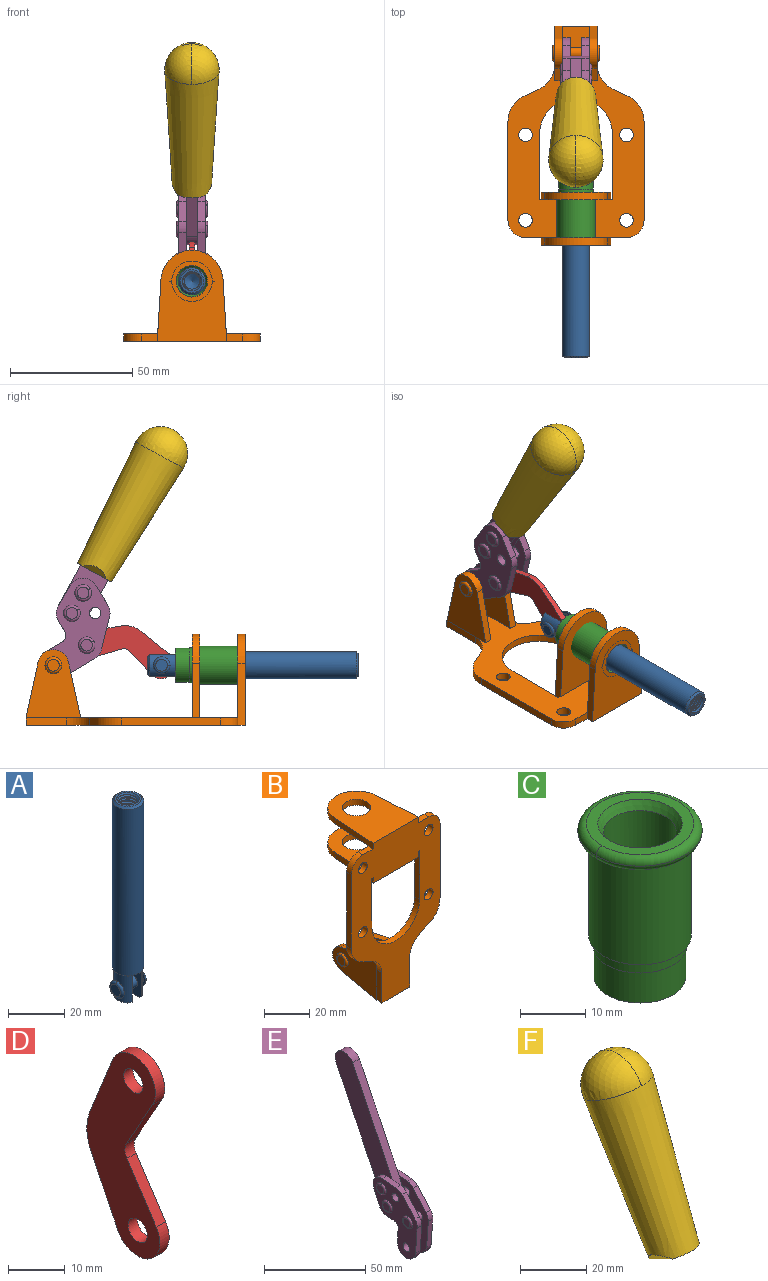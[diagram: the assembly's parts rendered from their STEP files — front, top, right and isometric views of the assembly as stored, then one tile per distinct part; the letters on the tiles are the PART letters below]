
ASSEMBLY  parts=6 mates=6
PART A: 48 faces, bbox 12.6x11.1x86.1 mm
  f0: torus R=2.41mm, axis (-1,0,0), area 15mm2, adj f30,f32,f34
  f1: torus R=2.41mm, axis (-1,0,0), area 15mm2, adj f29,f31,f33
  f2: cylinder r=5.54mm len=72.39mm, axis (0,0,1), area 2518.5mm2, adj f3,f4,f42,f43
  f3: cone r=5.54mm half-angle=45deg, axis (0,0,1), area 7.6mm2, adj f2,f5,f41
  f4: cone r=5.54mm half-angle=45deg, axis (0,0,-1), area 34.9mm2, adj f2,f39
  f5: cylinder r=5.08mm len=11.48mm, axis (0,0,1), area 108.3mm2, adj f3,f7,f8,f41
  f6: cylinder r=2.41mm len=4.83mm, axis (-1,0,0), area 71.2mm2, adj f40,f41
  f7: cylinder r=2.41mm len=4.83mm, axis (-1,0,0), area 7.6mm2, adj f5,f34
  f8: cone r=5.08mm half-angle=45deg, axis (0,0,1), area 10.6mm2, adj f5,f37,f41
  f9: cone r=3.98mm half-angle=45deg, axis (0,0,1), area 17.6mm2, adj f27,f39,f45,f46,f47
  f10: cylinder r=2.41mm len=4.83mm, axis (-1,0,0), area 7.6mm2, adj f33,f38
  f11: cylinder r=3.2mm len=6.4mm, axis (0,0,1), area 78.4mm2, adj f12,f28,f44,f45,f47
  f12: cylinder r=3.2mm len=6.4mm, axis (0,0,1), area 10.5mm2, adj f11,f13,f45,f47
  f13: cylinder r=3.2mm len=6.4mm, axis (0,0,1), area 10.5mm2, adj f12,f14,f45,f47
  f14: cylinder r=3.2mm len=6.4mm, axis (0,0,1), area 10.5mm2, adj f13,f15,f45,f47
  f15: cylinder r=3.2mm len=6.4mm, axis (0,0,1), area 10.5mm2, adj f14,f16,f45,f47
  f16: cylinder r=3.2mm len=6.4mm, axis (0,0,1), area 10.5mm2, adj f15,f17,f45,f47
  f17: cylinder r=3.2mm len=6.4mm, axis (0,0,1), area 10.5mm2, adj f16,f18,f45,f47
  f18: cylinder r=3.2mm len=6.4mm, axis (0,0,1), area 10.5mm2, adj f17,f19,f45,f47
  f19: cylinder r=3.2mm len=6.4mm, axis (0,0,1), area 10.5mm2, adj f18,f20,f45,f47
  f20: cylinder r=3.2mm len=6.4mm, axis (0,0,1), area 10.5mm2, adj f19,f21,f45,f47
  f21: cylinder r=3.2mm len=6.4mm, axis (0,0,1), area 10.5mm2, adj f20,f22,f45,f47
  f22: cylinder r=3.2mm len=6.4mm, axis (0,0,1), area 10.5mm2, adj f21,f23,f45,f47
  f23: cylinder r=3.2mm len=6.4mm, axis (0,0,1), area 10.5mm2, adj f22,f24,f45,f47
  f24: cylinder r=3.2mm len=6.4mm, axis (0,0,1), area 10.5mm2, adj f23,f25,f45,f47
  f25: cylinder r=3.2mm len=6.4mm, axis (0,0,1), area 10.5mm2, adj f24,f26,f45,f47
  f26: cylinder r=3.2mm len=6.4mm, axis (0,0,1), area 10.5mm2, adj f25,f27,f45,f47
  f27: cylinder r=3.2mm len=6.4mm, axis (0,0,1), area 7.4mm2, adj f9,f26,f45,f47
  f28: cone r=3.2mm half-angle=60deg, axis (0,0,1), area 37.2mm2, adj f11
  f29: plane 4.83x4.83mm, normal (-1,0,0), area 18.3mm2, adj f1,f31
  f30: plane 4.83x4.83mm, normal (1,0,0), area 18.3mm2, adj f0,f32
  f31: torus R=2.41mm, axis (-1,0,0), area 15mm2, adj f1,f29,f33
  f32: torus R=2.41mm, axis (-1,0,0), area 15mm2, adj f0,f30,f34
  f33: plane 6.83x6.83mm, normal (1,0,0), area 18.3mm2, adj f1,f10,f31
  f34: plane 6.83x6.83mm, normal (-1,0,0), area 18.3mm2, adj f0,f7,f32
  f35: cone r=5.08mm half-angle=45deg, axis (0,0,1), area 10.6mm2, adj f36,f38,f40
  f36: plane 7.25x1.97mm, normal (0,0,-1), area 10mm2, adj f35,f40
  f37: plane 7.25x1.97mm, normal (0,0,-1), area 10mm2, adj f8,f41
  f38: cylinder r=5.08mm len=11.48mm, axis (0,0,1), area 108.3mm2, adj f10,f35,f40,f42
  f39: plane 9.55x9.55mm, normal (0,0,1), area 22mm2, adj f4,f9
  f40: plane 12.76x10.09mm, normal (1,0,0), area 95.7mm2, adj f6,f35,f36,f38,f42,f43
  f41: plane 12.76x10.09mm, normal (-1,0,0), area 95.7mm2, adj f3,f5,f6,f8,f37,f43
  f42: cone r=5.54mm half-angle=45deg, axis (0,0,1), area 7.6mm2, adj f2,f38,f40
  f43: plane 11.07x4.7mm, normal (0,0,-1), area 50.4mm2, adj f2,f40,f41
  f44: plane 0.89x0.62mm, normal (-1,0,0), area 0.3mm2, adj f11,f45,f46,f47
  f45: bspline ~24.8x7.63mm, area 266.6mm2, adj f9,f11,f12,f13,f14,f15,f16,f17
  f46: bspline ~24.87x7.63mm, area 73.6mm2, adj f9,f44,f45,f47
  f47: bspline ~24.98x7.63mm, area 272.5mm2, adj f9,f11,f12,f13,f14,f15,f16,f17
PART B: 55 faces, bbox 55.7x37.4x89.8 mm
  f0: torus R=2.41mm, axis (-1,0,0), area 15mm2, adj f11,f15,f25
  f1: torus R=2.41mm, axis (-1,0,0), area 15mm2, adj f10,f12,f22
  f2: cylinder r=2.78mm len=5.56mm, axis (0,-1,0), area 54.2mm2, adj f30,f54
  f3: cylinder r=14.99mm len=29.97mm, axis (0,-1,0), area 145.9mm2, adj f30,f49,f53,f54
  f4: cylinder r=2.78mm len=5.56mm, axis (0,-1,0), area 54.2mm2, adj f30,f54
  f5: cylinder r=2.78mm len=5.56mm, axis (0,-1,0), area 54.2mm2, adj f30,f54
  f6: cylinder r=2.78mm len=5.56mm, axis (0,-1,0), area 54.2mm2, adj f30,f54
  f7: cylinder r=6.35mm len=12.7mm, axis (0,0,1), area 123.6mm2, adj f27,f51
  f8: cylinder r=6.35mm len=12.7mm, axis (0,0,-1), area 124.7mm2, adj f21,f35
  f9: cylinder r=2.41mm len=11.18mm, axis (-1,0,0), area 169.4mm2, adj f16,f19
  f10: plane 4.83x4.83mm, normal (1,0,0), area 18.3mm2, adj f1,f12
  f11: plane 4.83x4.83mm, normal (-1,0,0), area 18.3mm2, adj f0,f15
  f12: torus R=2.41mm, axis (-1,0,0), area 15mm2, adj f1,f10,f22
  f13: cylinder r=6.35mm len=12.41mm, axis (1,0,0), area 53.4mm2, adj f18,f19,f22,f23
  f14: cylinder r=6.35mm len=12.41mm, axis (-1,0,0), area 53.4mm2, adj f16,f17,f24,f25
  f15: torus R=2.41mm, axis (-1,0,0), area 15mm2, adj f0,f11,f25
  f16: plane 27.86x22.35mm, normal (1,0,0), area 425.4mm2, adj f9,f14,f17,f24,f30
  f17: plane 22.86x4.97mm, normal (0,0.21,0.98), area 72.5mm2, adj f14,f16,f25,f30
  f18: plane 22.86x4.97mm, normal (0,0.21,0.98), area 72.5mm2, adj f13,f19,f22,f30
  f19: plane 27.86x22.35mm, normal (-1,0,0), area 425.4mm2, adj f9,f13,f18,f23,f30
  f20: cylinder r=12.7mm len=25.35mm, axis (0,0,-1), area 119.8mm2, adj f21,f34,f35,f36
  f21: plane 34.21x28.07mm, normal (0,0,-1), area 702.4mm2, adj f8,f20,f30,f34,f36
  f22: plane 27.96x22.45mm, normal (1,0,0), area 407.2mm2, adj f1,f12,f13,f18,f23,f30,f42,f43
  f23: plane 22.86x4.97mm, normal (0,0.21,-0.98), area 72.5mm2, adj f13,f19,f22,f44
  f24: plane 22.86x4.97mm, normal (0,0.21,-0.98), area 72.5mm2, adj f14,f16,f25,f44
  f25: plane 27.86x22.35mm, normal (-1,0,0), area 407.1mm2, adj f0,f14,f15,f17,f24,f30,f45,f46
  f26: plane 3.1x0.95mm, normal (0,0,-1), area 2.7mm2, adj f30,f49,f50,f54
  f27: plane 34.21x28.07mm, normal (0,0,1), area 702.4mm2, adj f7,f28,f30,f50,f52
  f28: cylinder r=12.7mm len=25.35mm, axis (0,0,1), area 118.8mm2, adj f27,f50,f51,f52
  f29: plane 3.1x0.95mm, normal (0,0,-1), area 2.7mm2, adj f30,f52,f53,f54
  f30: plane 86.54x55.63mm, normal (0,1,0), area 2362.9mm2, adj f2,f3,f4,f5,f6,f16,f17,f18
  f31: plane 40.56x3.1mm, normal (-1,0,0), area 125.7mm2, adj f30,f32,f48,f54
  f32: cylinder r=7.11mm len=7.11mm, axis (0,-1,0), area 34.6mm2, adj f30,f31,f33,f54
  f33: plane 6.67x3.1mm, normal (0,0,1), area 20.4mm2, adj f30,f32,f34,f54
  f34: plane 25.39x3.13mm, normal (-1,0.06,0), area 79.5mm2, adj f20,f21,f33,f35,f54
  f35: plane 37.31x28.45mm, normal (0,0,1), area 789.9mm2, adj f8,f20,f34,f36,f54
  f36: plane 25.39x3.13mm, normal (1,0.06,0), area 79.5mm2, adj f20,f21,f35,f37,f54
  f37: plane 6.67x3.1mm, normal (0,0,1), area 20.4mm2, adj f30,f36,f38,f54
  f38: cylinder r=7.11mm len=7.11mm, axis (0,-1,0), area 34.6mm2, adj f30,f37,f39,f54
  f39: plane 40.56x3.1mm, normal (1,0,0), area 125.7mm2, adj f30,f38,f40,f54
  f40: cylinder r=11.18mm len=10.16mm, axis (0,-1,0), area 39.5mm2, adj f30,f39,f41,f54
  f41: plane 6.09x3.1mm, normal (0.42,0,-0.91), area 20.8mm2, adj f30,f40,f42,f54
  f42: cylinder r=11.18mm len=9.41mm, axis (0,-1,0), area 37.2mm2, adj f22,f30,f41,f43,f54
  f43: plane 16.5x3.1mm, normal (1,0,0), area 51.1mm2, adj f22,f42,f44,f54
  f44: plane 17.37x3.1mm, normal (0,0,-1), area 53.8mm2, adj f23,f24,f30,f43,f45,f54
  f45: plane 16.5x3.1mm, normal (-1,0,0), area 51.1mm2, adj f25,f44,f46,f54
  f46: cylinder r=11.18mm len=9.41mm, axis (0,-1,0), area 37.2mm2, adj f25,f30,f45,f47,f54
  f47: plane 6.09x3.1mm, normal (-0.42,0,-0.91), area 20.8mm2, adj f30,f46,f48,f54
  f48: cylinder r=11.18mm len=10.16mm, axis (0,-1,0), area 39.5mm2, adj f30,f31,f47,f54
  f49: plane 26.54x3.1mm, normal (-1,0,0), area 82.3mm2, adj f3,f26,f30,f54
  f50: plane 25.39x3.1mm, normal (1,0.06,0), area 78.8mm2, adj f26,f27,f28,f51,f54
  f51: plane 37.31x28.45mm, normal (0,0,-1), area 789.9mm2, adj f7,f28,f50,f52,f54
  f52: plane 25.39x3.1mm, normal (-1,0.06,0), area 78.8mm2, adj f27,f28,f29,f51,f54
  f53: plane 26.54x3.1mm, normal (1,0,0), area 82.3mm2, adj f3,f29,f30,f54
  f54: plane 89.66x55.63mm, normal (0,-1,0), area 2678.5mm2, adj f2,f3,f4,f5,f6,f26,f29,f31
PART C: 15 faces, bbox 20.6x20.6x28.7 mm
  f0: torus R=8.26mm, axis (0,0,1), area 56.8mm2, adj f1,f10,f12
  f1: torus R=8.26mm, axis (0,0,1), area 56.8mm2, adj f0,f6,f13
  f2: cylinder r=5.59mm len=25.91mm, axis (0,0,1), area 909.6mm2, adj f3,f4
  f3: cone r=6.86mm half-angle=45deg, axis (0,0,-1), area 70.2mm2, adj f2,f14
  f4: cone r=6.47mm half-angle=30deg, axis (0,0,1), area 66.7mm2, adj f2,f13
  f5: cylinder r=7.04mm len=14.07mm, axis (0,0,1), area 252.6mm2, adj f11,f14
  f6: torus R=8.26mm, axis (0,0,1), area 56.8mm2, adj f1,f12,f13
  f7: cylinder r=7.16mm len=14.33mm, axis (0,0,1), area 91.5mm2, adj f9,f11
  f8: cylinder r=7.86mm len=18.42mm, axis (0,0,1), area 909.6mm2, adj f9,f10
  f9: plane 15.72x15.72mm, normal (0,0,-1), area 33mm2, adj f7,f8
  f10: plane 16.51x16.51mm, normal (0,0,-1), area 19.9mm2, adj f0,f8,f12
  f11: plane 14.33x14.33mm, normal (0,0,-1), area 5.7mm2, adj f5,f7
  f12: torus R=8.26mm, axis (0,0,1), area 56.8mm2, adj f0,f6,f10
  f13: plane 16.51x16.51mm, normal (0,0,1), area 82.7mm2, adj f1,f4,f6
  f14: plane 14.07x14.07mm, normal (0,0,-1), area 7.8mm2, adj f3,f5
PART D: 12 faces, bbox 2.3x18.2x42.8 mm
  f0: cylinder r=2.4mm len=4.8mm, axis (1,0,0), area 34.9mm2, adj f4,f11
  f1: cylinder r=10.41mm len=8.47mm, axis (1,0,0), area 20.2mm2, adj f4,f9,f10,f11
  f2: cylinder r=3.05mm len=3.16mm, axis (1,0,0), area 7.7mm2, adj f4,f6,f7,f11
  f3: cylinder r=2.4mm len=4.8mm, axis (1,0,0), area 34.9mm2, adj f4,f11
  f4: plane 42.81x18.23mm, normal (-1,0,0), area 414.1mm2, adj f0,f1,f2,f3,f5,f6,f7,f8
  f5: cylinder r=5.54mm len=10.67mm, axis (1,0,0), area 41.8mm2, adj f4,f6,f10,f11
  f6: plane 11.66x6.53mm, normal (0,-0.87,-0.49), area 30.9mm2, adj f2,f4,f5,f11
  f7: plane 11.17x7.33mm, normal (0,-0.84,0.55), area 30.9mm2, adj f2,f4,f8,f11
  f8: cylinder r=5.54mm len=10.51mm, axis (1,0,0), area 41.8mm2, adj f4,f7,f9,f11
  f9: plane 13.67x6.67mm, normal (0,0.9,-0.44), area 35.1mm2, adj f1,f4,f8,f11
  f10: plane 14.1x5.7mm, normal (0,0.93,0.37), area 35.1mm2, adj f1,f4,f5,f11
  f11: plane 42.81x18.23mm, normal (1,0,0), area 414.1mm2, adj f0,f1,f2,f3,f5,f6,f7,f8
PART E: 59 faces, bbox 12.9x60.2x99.6 mm
  f0: torus R=2.39mm, axis (-1,0,0), area 14.9mm2, adj f20,f43,f51
  f1: torus R=2.39mm, axis (-1,0,0), area 14.9mm2, adj f19,f42,f51
  f2: torus R=2.39mm, axis (-1,0,0), area 14.9mm2, adj f18,f35,f51
  f3: torus R=2.39mm, axis (-1,0,0), area 14.9mm2, adj f14,f17,f23
  f4: torus R=2.39mm, axis (-1,0,0), area 14.9mm2, adj f13,f16,f23
  f5: torus R=2.39mm, axis (-1,0,0), area 14.9mm2, adj f12,f15,f23
  f6: cylinder r=2.39mm len=4.78mm, axis (1,0,0), area 46.5mm2, adj f48,f50,f51
  f7: cylinder r=2.39mm len=4.78mm, axis (1,0,0), area 46.5mm2, adj f50,f51
  f8: cylinder r=6.35mm len=12.68mm, axis (1,0,0), area 61.8mm2, adj f38,f39,f50,f51
  f9: cylinder r=2.39mm len=4.78mm, axis (-1,0,0), area 70.5mm2, adj f46,f50
  f10: cylinder r=2.39mm len=4.78mm, axis (-1,0,0), area 46.5mm2, adj f23,f45,f46
  f11: cylinder r=2.39mm len=4.78mm, axis (-1,0,0), area 46.5mm2, adj f23,f46
  f12: plane 4.78x4.78mm, normal (1,0,0), area 17.9mm2, adj f5,f15
  f13: plane 4.78x4.78mm, normal (1,0,0), area 17.9mm2, adj f4,f16
  f14: plane 4.78x4.78mm, normal (1,0,0), area 17.9mm2, adj f3,f17
  f15: torus R=2.39mm, axis (-1,0,0), area 14.9mm2, adj f5,f12,f23
  f16: torus R=2.39mm, axis (-1,0,0), area 14.9mm2, adj f4,f13,f23
  f17: torus R=2.39mm, axis (-1,0,0), area 14.9mm2, adj f3,f14,f23
  f18: plane 4.78x4.78mm, normal (-1,0,0), area 17.9mm2, adj f2,f35
  f19: plane 4.78x4.78mm, normal (-1,0,0), area 17.9mm2, adj f1,f42
  f20: plane 4.78x4.78mm, normal (-1,0,0), area 17.9mm2, adj f0,f43
  f21: plane 2.26x0.2mm, normal (1,0,0), area 0.2mm2, adj f31,f44
  f22: plane 2.26x0.2mm, normal (-1,0,0), area 0.2mm2, adj f41,f44
  f23: plane 39.37x30.77mm, normal (1,0,0), area 565.5mm2, adj f3,f4,f5,f10,f11,f15,f16,f17
  f24: cylinder r=6.1mm len=4.15mm, axis (-1,0,0), area 14.7mm2, adj f23,f25,f32,f46
  f25: plane 10.25x9.01mm, normal (0,-0.75,0.66), area 42.3mm2, adj f23,f24,f26,f46
  f26: cylinder r=6.35mm len=4.64mm, axis (-1,0,0), area 15.6mm2, adj f23,f25,f27,f46
  f27: plane 15.84x3.1mm, normal (0,-1,-0.07), area 49.2mm2, adj f23,f26,f28,f46
  f28: cylinder r=6.35mm len=12.68mm, axis (-1,0,0), area 61.8mm2, adj f23,f27,f29,f46
  f29: plane 8.11x3.1mm, normal (0,1,0.07), area 25.2mm2, adj f23,f28,f30,f46
  f30: cylinder r=3.05mm len=3.25mm, axis (-1,0,0), area 14.8mm2, adj f23,f29,f31,f46
  f31: plane 5.99x3.1mm, normal (0,0.07,-1), area 18.6mm2, adj f21,f23,f30,f44,f46
  f32: plane 9.5x3.1mm, normal (0,-0.07,1), area 29.5mm2, adj f23,f24,f33,f46,f47
  f33: cylinder r=6.1mm len=8.63mm, axis (-1,0,0), area 39.1mm2, adj f23,f32,f34,f47
  f34: plane 8.65x3.96mm, normal (0,0.91,-0.42), area 29.5mm2, adj f23,f33,f44,f47
  f35: torus R=2.39mm, axis (-1,0,0), area 14.9mm2, adj f2,f18,f51
  f36: plane 10.25x9.01mm, normal (0,-0.75,0.66), area 42.3mm2, adj f37,f49,f50,f51
  f37: cylinder r=6.35mm len=4.64mm, axis (1,0,0), area 15.6mm2, adj f36,f38,f50,f51
  f38: plane 15.84x3.1mm, normal (0,-1,-0.07), area 49.2mm2, adj f8,f37,f50,f51
  f39: plane 8.11x3.1mm, normal (0,1,0.07), area 25.2mm2, adj f8,f40,f50,f51
  f40: cylinder r=3.05mm len=3.25mm, axis (1,0,0), area 14.8mm2, adj f39,f41,f50,f51
  f41: plane 5.99x3.1mm, normal (0,0.07,-1), area 18.6mm2, adj f22,f40,f44,f50,f51
  f42: torus R=2.39mm, axis (-1,0,0), area 14.9mm2, adj f1,f19,f51
  f43: torus R=2.39mm, axis (-1,0,0), area 14.9mm2, adj f0,f20,f51
  f44: cylinder r=6.35mm len=12.12mm, axis (-1,0,0), area 128.9mm2, adj f21,f22,f23,f31,f34,f41,f46,f47
  f45: plane 2.65x1.35mm, normal (1,0,0), area 1mm2, adj f10,f55
  f46: plane 39.08x20.42mm, normal (-1,0,0), area 412.5mm2, adj f9,f10,f11,f24,f25,f26,f27,f28
  f47: plane 77.62x39.82mm, normal (1,0,0), area 850mm2, adj f32,f33,f34,f44,f53,f54,f55
  f48: plane 2.65x1.35mm, normal (-1,0,0), area 1mm2, adj f6,f55
  f49: cylinder r=6.1mm len=4.15mm, axis (1,0,0), area 14.7mm2, adj f36,f50,f51,f56
  f50: plane 39.08x20.42mm, normal (1,0,0), area 412.5mm2, adj f6,f7,f8,f9,f36,f37,f38,f39
  f51: plane 39.37x30.77mm, normal (-1,0,0), area 565.5mm2, adj f0,f1,f2,f6,f7,f8,f35,f36
  f52: plane 8.65x3.96mm, normal (0,0.91,-0.42), area 29.5mm2, adj f44,f51,f57,f58
  f53: plane 68.49x33.4mm, normal (0,0.9,-0.44), area 358.1mm2, adj f44,f47,f54,f58
  f54: cylinder r=6.35mm len=12.06mm, axis (1,0,0), area 93.7mm2, adj f47,f53,f55,f58
  f55: plane 68.49x33.4mm, normal (0,-0.9,0.44), area 358.1mm2, adj f44,f45,f46,f47,f48,f50,f54,f58
  f56: plane 9.5x3.1mm, normal (0,-0.07,1), area 29.5mm2, adj f49,f50,f51,f57,f58
  f57: cylinder r=6.1mm len=8.63mm, axis (1,0,0), area 39.1mm2, adj f51,f52,f56,f58
  f58: plane 77.62x39.82mm, normal (-1,0,0), area 850mm2, adj f44,f52,f53,f54,f55,f56,f57
PART F: 11 faces, bbox 22.3x42.6x64.5 mm
  f0: sphere r=11.13mm, area 411.4mm2, adj f1,f8
  f1: cone r=11.11mm half-angle=3.3deg, axis (0,0.44,0.9), area 3251.8mm2, adj f0,f7,f8,f9,f10
  f2: cylinder r=6.16mm len=11.7mm, axis (1,0,0), area 89.5mm2, adj f3,f4,f5,f6
  f3: plane 60.23x36.75mm, normal (-1,0,0), area 763.6mm2, adj f2,f4,f6,f10
  f4: plane 51.37x25.05mm, normal (0,0.9,-0.44), area 264.2mm2, adj f2,f3,f5,f10
  f5: plane 60.23x36.75mm, normal (1,0,0), area 763.6mm2, adj f2,f4,f6,f10
  f6: plane 51.37x25.05mm, normal (0,-0.9,0.44), area 264.2mm2, adj f2,f3,f5,f10
  f7: plane 9.95x5.95mm, normal (0.71,-0.31,-0.64), area 25.8mm2, adj f1,f10
  f8: sphere r=11.13mm, area 411.4mm2, adj f0,f1
  f9: plane 9.95x5.95mm, normal (-0.71,-0.31,-0.64), area 25.8mm2, adj f1,f10
  f10: plane 14.27x11.38mm, normal (0,-0.44,-0.9), area 106.7mm2, adj f1,f3,f4,f5,f6,f7,f9
PLACE A rot(axis=(1,0,0),90deg) t=(0,4.51,-3.1)mm
PLACE B rot(axis=(1,0,0),90deg) t=(0,1.23,-3.1)mm fixed
PLACE C rot(axis=(1,0,0),90deg) t=(0,3.77,-3.1)mm
PLACE D rot(axis=(1,0,0),106.9deg) t=(0,11.01,2.47)mm
PLACE E rot(axis=(1,0,0),55deg) t=(0,-7.08,19.76)mm
PLACE F rot(axis=(1,0,0),55deg) t=(-0.04,-7.08,19.76)mm
MATE fastened F.f2 <-> E.f54  axis (1,0,0) through (-2.35,-11.2,109.37)mm
MATE revolute B.f0 <-> E.f7  axis (-1,0,0) through (0,33.32,21.51)mm
MATE slider A.f2 <-> B.f7  axis (0,-1,0) through (0,-54.27,21.51)mm
MATE fastened C.f2 <-> B.f7  axis (0,-1,0) through (0,-45.16,21.51)mm
MATE revolute D.f3 <-> E.f4  axis (1,0,0) through (0,19.72,29.69)mm
MATE revolute D.f5 <-> A.f6  axis (1,0,0) through (0,-10.96,21.51)mm
